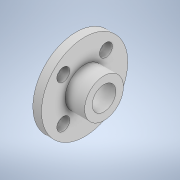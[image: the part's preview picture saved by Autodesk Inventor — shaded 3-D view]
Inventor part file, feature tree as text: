
AUTODESK INVENTOR PART (.ipt)
format: ipt  version: 2020 (Build 240168000, 168)  size: 136,704 bytes
history: native  units: in
note: dims shown in document units (in); Inventor stores cm internally (conversion verified against a paired STEP export)
features: extrude x2, sketch x2
ambient origin geometry x8: Origin, YZ Plane, XZ Plane, XY Plane, X Axis, Y Axis, Z Axis, Center Point
bodies: Solid1 (feature_tree)
feature tree (4):
  extrude  "Extrusion1"  Depth=0.1181in
  extrude  "Extrusion2"  Depth=0.1772in
  sketch  "Sketch1"  dims[d0=0.7874in d1=0.1181in]
  sketch  "Sketch2"  dims[d2=0.1181in d3=0.1181in d4=0.1181in d7=0.5512in d8=0.0787in d9=0.0in d10=0.1181in d11=0.2165in d12=0.3543in d13=0.1772in d14=0.0in]
